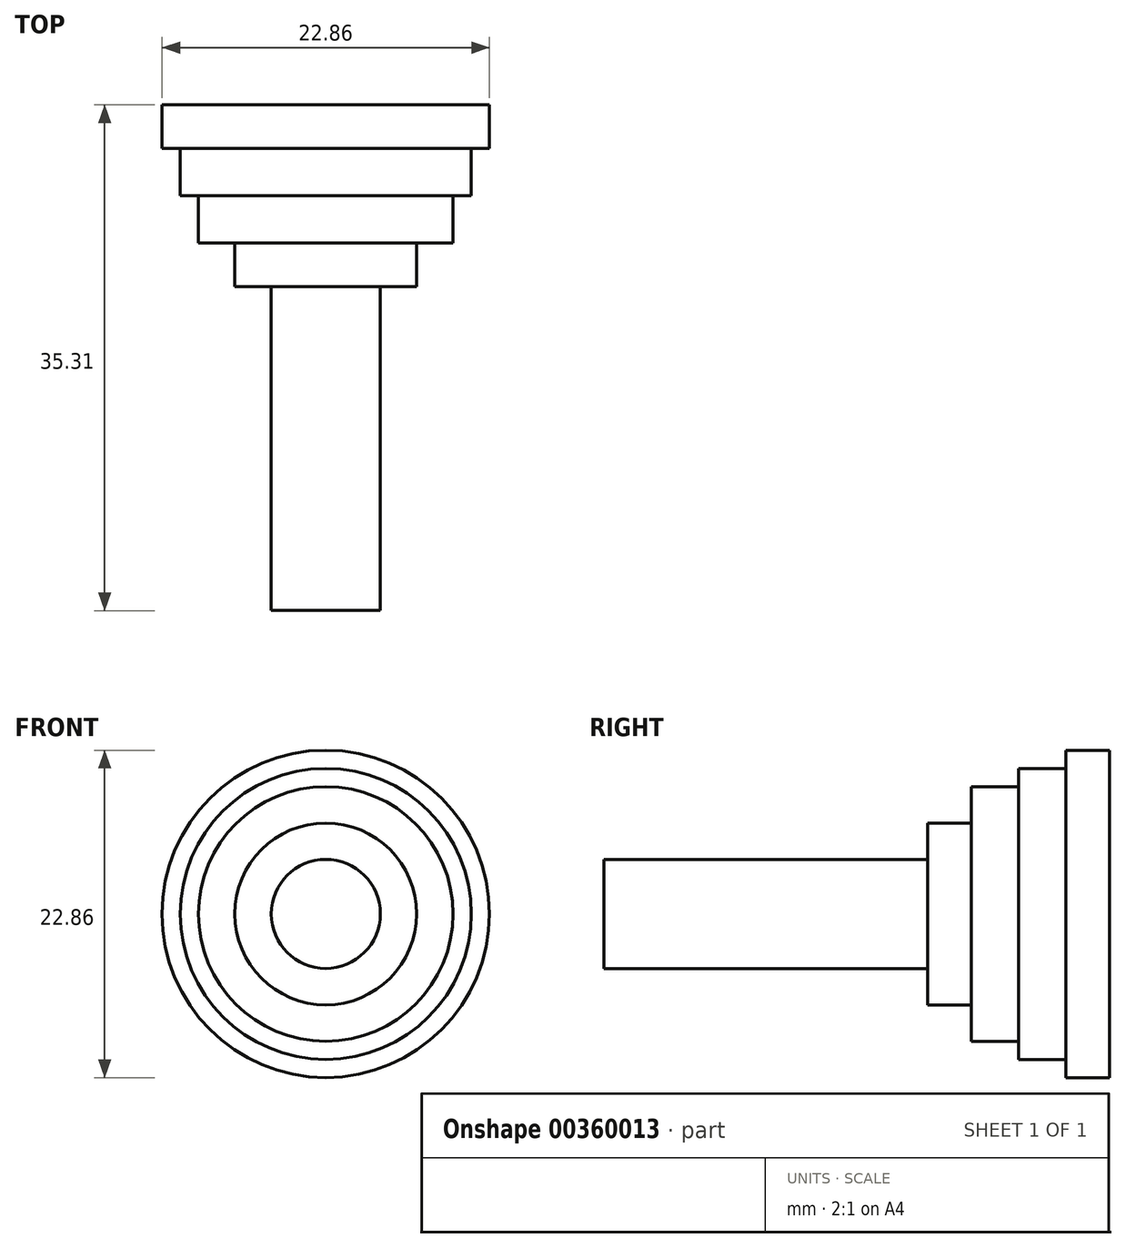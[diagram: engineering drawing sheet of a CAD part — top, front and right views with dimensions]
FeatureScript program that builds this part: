
annotation { "Feature Type Name" : "Feature", "Feature Type Description" : "" }
export const myFeature = defineFeature(function(context is Context, id is Id, definition is map)
    precondition{}
    {
        {
            var Q0;
            Q0=qCreatedBy(makeId("Front.planeOp"),FACE);
            var sketch = newSketch(context, id + "F0", { "sketchPlane" : qUnion([Q0])});
            skCircle(sketch, "E0", {"center": v(0, 0) * mm, "radius": 3.81 * mm});
            skSolve(sketch);
        }
        {
            var Q0;
            Q0=makeQuery(id+"F0.imprint","IMPRINT",FACE,{"disambiguationData":[TD([[makeQuery(id+"F0.imprint","IMPRINT",EDGE,{"derivedFrom":sQuery(id+"F0.wireOp",EDGE,"E0")}),1.0]])]});
            extrude(context, id + "F1", {"entities" : qUnion([Q0]), "depth" : 35.3 * mm});
        }
        {
            var Q0;
            Q0=qCreatedBy(makeId("Front.planeOp"),FACE);
            var sketch = newSketch(context, id + "F2", { "sketchPlane" : qUnion([Q0])});
            skCircle(sketch, "E1", {"center": v(0, 0) * mm, "radius": 6.35 * mm});
            skSolve(sketch);
        }
        {
            var Q0;
            Q0=makeQuery(id+"F2.imprint","IMPRINT",FACE,{"disambiguationData":[TD([[makeQuery(id+"F2.imprint","IMPRINT",EDGE,{"derivedFrom":sQuery(id+"F2.wireOp",EDGE,"E1")}),1.0]])]});
            extrude(context, id + "F3", {"entities" : qUnion([Q0]), "operationType" : NewBodyOperationType.ADD, "depth" : 12.7 * mm});
        }
        {
            var Q0;
            Q0=qCreatedBy(makeId("Front.planeOp"),FACE);
            var sketch = newSketch(context, id + "F4", { "sketchPlane" : qUnion([Q0])});
            skCircle(sketch, "E2", {"center": v(0, 0) * mm, "radius": 8.9 * mm});
            skSolve(sketch);
        }
        {
            var Q0;
            Q0=makeQuery(id+"F4.imprint","IMPRINT",FACE,{"disambiguationData":[TD([[makeQuery(id+"F4.imprint","IMPRINT",EDGE,{"derivedFrom":sQuery(id+"F4.wireOp",EDGE,"E2")}),1.0]])]});
            extrude(context, id + "F5", {"entities" : qUnion([Q0]), "operationType" : NewBodyOperationType.ADD, "depth" : 9.65 * mm});
        }
        {
            var Q0;
            Q0=qCreatedBy(makeId("Front.planeOp"),FACE);
            var sketch = newSketch(context, id + "F6", { "sketchPlane" : qUnion([Q0])});
            skCircle(sketch, "E3", {"center": v(0, 0) * mm, "radius": 10.16 * mm});
            skSolve(sketch);
        }
        {
            var Q0;
            Q0=makeQuery(id+"F6.imprint","IMPRINT",FACE,{"disambiguationData":[TD([[makeQuery(id+"F6.imprint","IMPRINT",EDGE,{"derivedFrom":sQuery(id+"F6.wireOp",EDGE,"E3")}),1.0]])]});
            extrude(context, id + "F7", {"entities" : qUnion([Q0]), "operationType" : NewBodyOperationType.ADD, "depth" : 6.35 * mm});
        }
        {
            var Q0;
            Q0=qCreatedBy(makeId("Front.planeOp"),FACE);
            var sketch = newSketch(context, id + "F8", { "sketchPlane" : qUnion([Q0])});
            skCircle(sketch, "E4", {"center": v(0, 0) * mm, "radius": 11.43 * mm});
            skSolve(sketch);
        }
        {
            var Q0;
            Q0=makeQuery(id+"F8.imprint","IMPRINT",FACE,{"disambiguationData":[TD([[makeQuery(id+"F8.imprint","IMPRINT",EDGE,{"derivedFrom":sQuery(id+"F8.wireOp",EDGE,"E4")}),1.0]])]});
            extrude(context, id + "F9", {"entities" : qUnion([Q0]), "operationType" : NewBodyOperationType.ADD, "depth" : 3.05 * mm});
        }
        {
            var Q0;
            Q0=qCreatedBy(makeId("Top.planeOp"),FACE);
            var sketch = newSketch(context, id + "F10", { "sketchPlane" : qUnion([Q0])});
            skLineSegment(sketch, "E5", {"start": v(0, -43.7) * mm, "end": v(-6.29, -43.7) * mm, "construction": true});
            skLineSegment(sketch, "E6", {"start": v(0, -43.7) * mm, "end": v(0, -53.85) * mm, "construction": true});
            skArc(sketch, "E7", {"start": v(-6.29, -43.7) * mm, "mid": v(-4.6, -49.68) * mm, "end": v(0, -53.85) * mm});
            skSolve(sketch);
        }
        {
            var Q0;
            Q0=sQuery(id+"F10.wireOp",EDGE,"E7");
            var Q1;
            Q1=sQuery(id+"F10.wireOp",EDGE,"E6");
            revolve(context, id + "F11", {"bodyType" : ToolBodyType.SURFACE, "surfaceEntities" : qUnion([Q0]), "axis" : qUnion([Q1]), "revolveType" : RevolveType.FULL});
        }
        {
            var Q0;
            Q0=qCreatedBy(makeId("Top.planeOp"),FACE);
            var sketch = newSketch(context, id + "F12", { "sketchPlane" : qUnion([Q0])});
            skLineSegment(sketch, "E8", {"start": v(0, -51.73) * mm, "end": v(0, -57.31) * mm, "construction": true});
            skLineSegment(sketch, "E9", {"start": v(0, -51.73) * mm, "end": v(0, -51.73) * mm});
            skArc(sketch, "E10", {"start": v(0, -51.73) * mm, "mid": v(-2.8, -54.52) * mm, "end": v(0, -57.31) * mm});
            skPoint(sketch, "E11", {"position": v(0, -51.73) * mm});
            skSolve(sketch);
        }
        {
            var Q0;
            Q0=sQuery(id+"F12.wireOp",EDGE,"E10");
            var Q1;
            Q1=sQuery(id+"F12.wireOp",EDGE,"E8");
            revolve(context, id + "F13", {"bodyType" : ToolBodyType.SURFACE, "operationType" : NewBodyOperationType.ADD, "surfaceEntities" : qUnion([Q0]), "axis" : qUnion([Q1]), "revolveType" : RevolveType.FULL});
        }
        {
            var Q0;
            Q0=qCreatedBy(makeId("Top.planeOp"),FACE);
            var sketch = newSketch(context, id + "F14", { "sketchPlane" : qUnion([Q0])});
            skLineSegment(sketch, "E12", {"start": v(0, -43.66) * mm, "end": v(0, -21.1) * mm, "construction": true});
            skLineSegment(sketch, "E13", {"start": v(0, -43.66) * mm, "end": v(-7.58, -43.66) * mm});
            skLineSegment(sketch, "E14", {"start": v(-7.58, -43.66) * mm, "end": v(0, -21.1) * mm});
            skSolve(sketch);
        }
        {
            var Q0;
            Q0=sQuery(id+"F14.wireOp",EDGE,"E13");
            var Q1;
            Q1=sQuery(id+"F14.wireOp",EDGE,"E14");
            var Q2;
            Q2=sQuery(id+"F14.wireOp",EDGE,"E12");
            revolve(context, id + "F15", {"bodyType" : ToolBodyType.SURFACE, "surfaceEntities" : qUnion([Q0, Q1]), "axis" : qUnion([Q2]), "revolveType" : RevolveType.FULL});
        }
        {
            var Q0;
            Q0=qCreatedBy(makeId("Top.planeOp"),FACE);
            var sketch = newSketch(context, id + "F16", { "sketchPlane" : qUnion([Q0])});
            skLineSegment(sketch, "E15", {"start": v(0, -37.85) * mm, "end": v(0, -32.03) * mm, "construction": true});
            skLineSegment(sketch, "E16", {"start": v(0, -32.03) * mm, "end": v(-7.36, -32.03) * mm});
            skLineSegment(sketch, "E17", {"start": v(-7.36, -32.03) * mm, "end": v(0, -37.85) * mm});
            skSolve(sketch);
        }
        {
            var Q0;
            Q0=sQuery(id+"F16.wireOp",EDGE,"E17");
            var Q1;
            Q1=sQuery(id+"F16.wireOp",EDGE,"E16");
            var Q2;
            Q2=sQuery(id+"F16.wireOp",EDGE,"E15");
            revolve(context, id + "F17", {"bodyType" : ToolBodyType.SURFACE, "surfaceEntities" : qUnion([Q0, Q1]), "axis" : qUnion([Q2]), "revolveType" : RevolveType.FULL});
        }
    });
